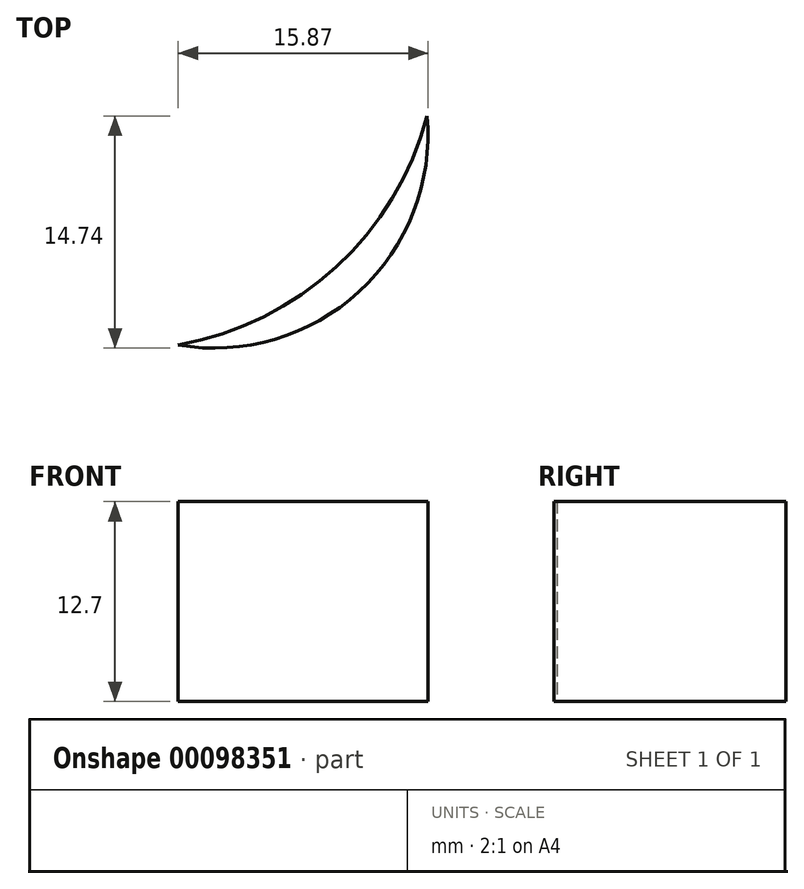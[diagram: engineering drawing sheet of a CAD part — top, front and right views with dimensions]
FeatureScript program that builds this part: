
annotation { "Feature Type Name" : "Feature", "Feature Type Description" : "" }
export const myFeature = defineFeature(function(context is Context, id is Id, definition is map)
    precondition{}
    {
        {
            var Q0;
            Q0=qCreatedBy(makeId("Top.planeOp"),FACE);
            var sketch = newSketch(context, id + "F0", { "sketchPlane" : qUnion([Q0])});
            skArc(sketch, "E0", {"start": v(-15.82, 2.36) * mm, "mid": v(-4.34, 5.75) * mm, "end": v(0, 16.91) * mm});
            skArc(sketch, "E1", {"start": v(-15.82, 2.36) * mm, "mid": v(-5.79, 7.33) * mm, "end": v(0, 16.91) * mm});
            skSolve(sketch);
        }
        {
            var Q0;
            Q0 = qSketchRegion(id + "F0", true);
            extrude(context, id + "F1", {"entities" : qUnion([Q0]), "depth" : 12.7 * mm});
        }
    });
